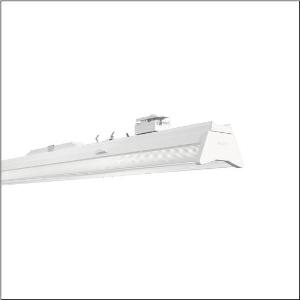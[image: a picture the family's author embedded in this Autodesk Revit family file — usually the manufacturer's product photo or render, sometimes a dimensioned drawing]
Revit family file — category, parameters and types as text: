
# Revit family: licross_r__21_performance_ho_52td16dn4e5m_0710
name_source: partatom
category: Lighting Fixtures
units: mm (PartAtom-declared; Revit-internal decimal feet)

## family parameters
Cut with Voids When Loaded = No
Host = Face
Light Source = No
Part Type = Normal
Room Calculation Point = No
Round Connector Dimension = Use Diameter
Shared = No

## types (1)
- --- (1 x LED, 14870 lm, 84.9 W, 4000K)
    Apparent Load = 85 VA
    CIE Flux Codes = 63 87 95 78 100
    Color Rendering = 80
    Color Temperature = 4000K
    Default Elevation = 1800 mm
    Description = Licross® 21 Performance HO, luminaire insert, of sheet steel, galvanised, coil coated, white, length: 1.500mm, width: 120mm, height: 123mm, LED rated luminous flux: 14.870lm, light colour: 840, control gear: DALI 2, with plug, 5-pole, with phase selection, mains connection: 220..240V, AC, 50/60Hz, rated input power: 85W, halogen-free wiring, primary light control with lens, of plastic, primary optical cover: cover, of PMMA, light emission: direct/indirect distribution, primary light characteristic: symmetric, protection rating (complete): IP54, insulation class (complete): insulation class I (protective earthing), certification: CE, ENEC, VDE, UKCA, protection symbol: D if used in an environment with non-conductive dust loads with corresponding accessories, impact resistance: IK06, permissible ambient temperature for indoor applications: -25..+35°C, corresponds to IFS (International Featured Standards) requirements for safety and quality in the food industry, reducing of maximum allowable ambient temperature of 5°C with ceiling mounting, LABS conformity tested according to VDMA 24364:2018-05, packaging unit: 1 piece
    Height = 114 mm
    Lamp = 1 x LED
    Lamp Light Flux = 14870 lm
    Lamp Power = 84.9 W
    Lamp count = 1
    Length = 1500 mm
    Luminous efficacy = 175 lm/W
    Manufacturer = Siteco
    ModVariant = No
    Model = 52TD16DN4E5M
    Mounting Place = Ceiling
    Mounting Type = Pendant
    Number of Poles = 1
    OnlyDefault = Yes
    Power Factor = 1
    Product Name = Licross® 21 Performance HO
    Product group = luminaire insert
    ProductGroupID = 901
    Protection Class = Protection class I
    Protection Degree = IP 54
    RLX_Detail_Level = 1
    RLX_Emergency_Light_Flux = 0 lm
    RLX_Emergency_Type = 0
    RLX_Emergency_Type_DB = No
    RlxData = <blob elided: 34021 chars, md5=31c1d2c4>
    Socket = socket
    Standby Power = 0 W
    System Light Flux = 14870 lm
    System Power = 85 W
    Type Comments = factory setting: luminous flux: 100 % | dim-lin: 254 | 484 mA
    Type Image = l_1256138.jpg
    URL = http://relux.com
    VarID = @adj_099649
    Voltage = 0 V
    Weight = 0.00 kg
    Width = 120 mm

## geometry (parser evidence)
native form markers: Blend x4, Sweep x11
no freeform markers — native parametric forms only
